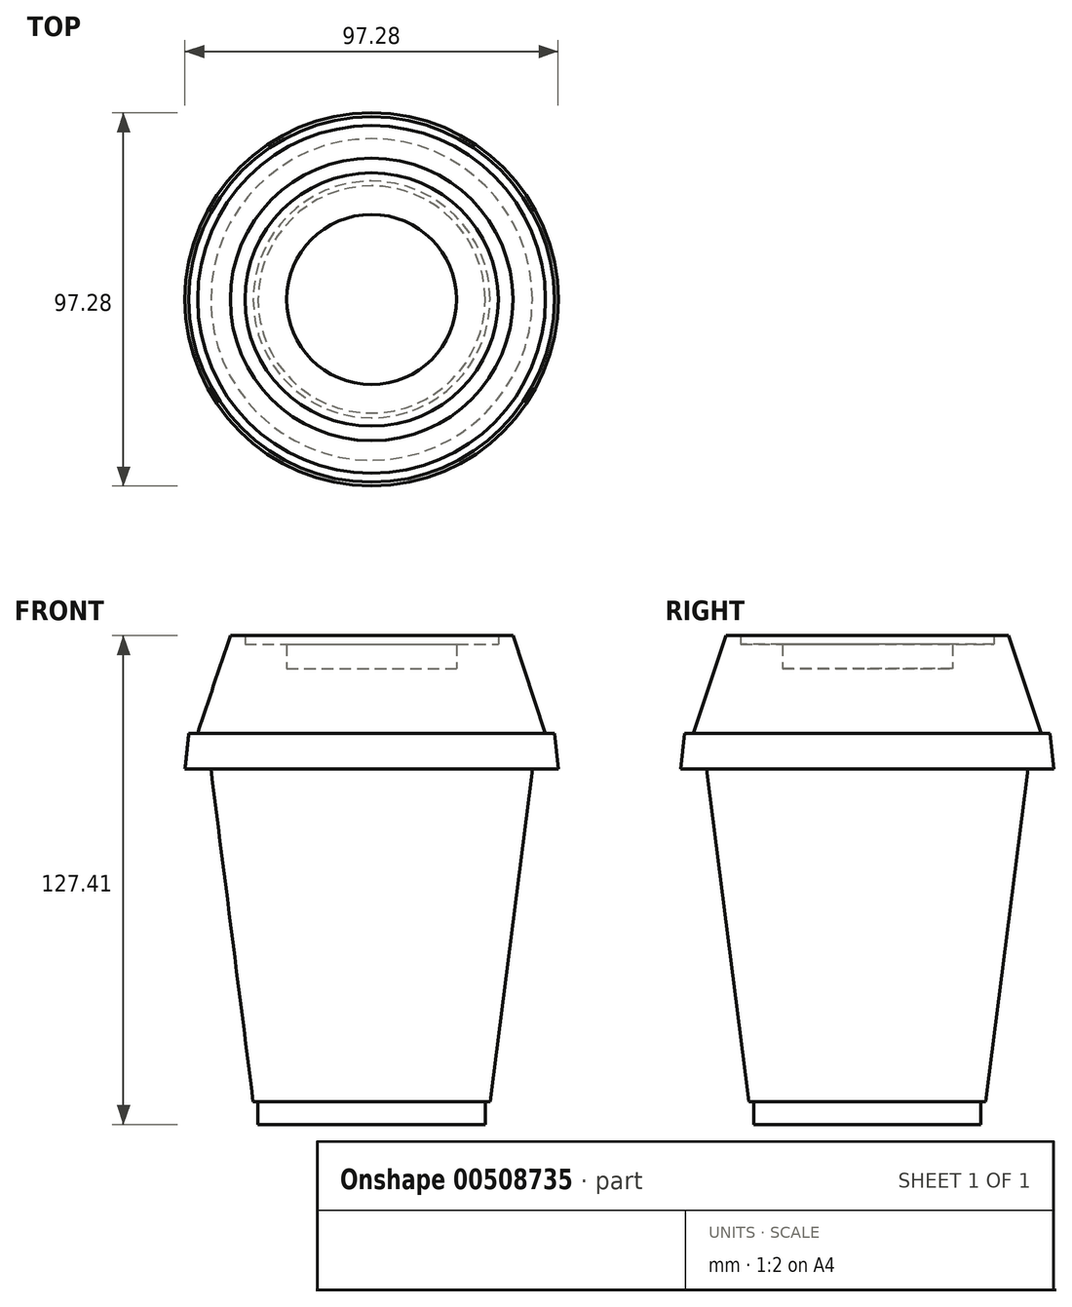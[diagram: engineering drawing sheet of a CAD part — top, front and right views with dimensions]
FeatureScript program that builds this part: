
annotation { "Feature Type Name" : "Feature", "Feature Type Description" : "" }
export const myFeature = defineFeature(function(context is Context, id is Id, definition is map)
    precondition{}
    {
        {
            var Q0;
            Q0=qCreatedBy(makeId("Front.planeOp"),FACE);
            var sketch = newSketch(context, id + "F0", { "sketchPlane" : qUnion([Q0])});
            skLineSegment(sketch, "E0", {"start": v(0, 0) * mm, "end": v(29.6, 0) * mm});
            skLineSegment(sketch, "E1", {"start": v(29.6, 0) * mm, "end": v(29.6, 5.87) * mm});
            skLineSegment(sketch, "E2", {"start": v(29.6, 5.87) * mm, "end": v(30.86, 5.87) * mm});
            skLineSegment(sketch, "E3", {"start": v(30.86, 5.87) * mm, "end": v(41.9, 92.71) * mm});
            skLineSegment(sketch, "E4", {"start": v(41.9, 92.71) * mm, "end": v(48.64, 92.71) * mm});
            skLineSegment(sketch, "E5", {"start": v(48.64, 92.7) * mm, "end": v(47.62, 101.98) * mm});
            skLineSegment(sketch, "E6", {"start": v(47.62, 101.98) * mm, "end": v(45.34, 101.98) * mm});
            skLineSegment(sketch, "E7", {"start": v(45.34, 101.98) * mm, "end": v(36.83, 127.4) * mm});
            skLineSegment(sketch, "E8", {"start": v(36.83, 127.4) * mm, "end": v(33.02, 127.4) * mm});
            skLineSegment(sketch, "E9", {"start": v(33.02, 127.4) * mm, "end": v(33.02, 125.12) * mm});
            skLineSegment(sketch, "E10", {"start": v(33.02, 125.12) * mm, "end": v(22.16, 125.12) * mm});
            skLineSegment(sketch, "E11", {"start": v(22.16, 125.12) * mm, "end": v(22.16, 118.77) * mm});
            skLineSegment(sketch, "E12", {"start": v(22.16, 118.77) * mm, "end": v(0, 118.77) * mm});
            skLineSegment(sketch, "E13", {"start": v(0, 118.77) * mm, "end": v(0, 0) * mm});
            skLineSegment(sketch, "E14", {"start": v(0, 0) * mm, "end": v(0, -18.01) * mm, "construction": true});
            skLineSegment(sketch, "E15", {"start": v(0, 118.77) * mm, "end": v(0, 143.34) * mm, "construction": true});
            skSolve(sketch);
        }
        {
            var Q0;
            Q0=makeQuery(id+"F0.imprint","IMPRINT",FACE,{"disambiguationData":[TD([[makeQuery(id+"F0.imprint","IMPRINT",EDGE,{"derivedFrom":sQuery(id+"F0.wireOp",EDGE,"E0")}),1.0]])]});
            var Q1;
            Q1=sQuery(id+"F0.wireOp",EDGE,"E15");
            revolve(context, id + "F1", {"entities" : qUnion([Q0]), "axis" : qUnion([Q1]), "revolveType" : RevolveType.FULL});
        }
    });
